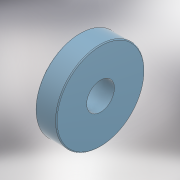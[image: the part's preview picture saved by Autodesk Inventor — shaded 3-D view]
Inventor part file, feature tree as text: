
AUTODESK INVENTOR PART (.ipt)
format: ipt  version: 2022 (Build 260153000, 153)  size: 145,920 bytes
history: native  units: mm
features: extrude x1, fillet x1, sketch x1
ambient origin geometry x8: Origin, YZ Plane, XZ Plane, XY Plane, X Axis, Y Axis, Z Axis, Center Point
bodies: Solid1 (feature_tree)
feature tree (3):
  extrude  "Extrusion1"  Depth=2.0mm
  fillet  "Fillet1"  [1 undecoded]
  sketch  "Sketch1"  dims[d0=50.0mm d1=0.0mm d2=2.0mm]
note: 1 required parameter value undecoded (feature->parameter linkage not recoverable at this tier; creation-order binding heuristic only, values carry confidence <= 0.55)
